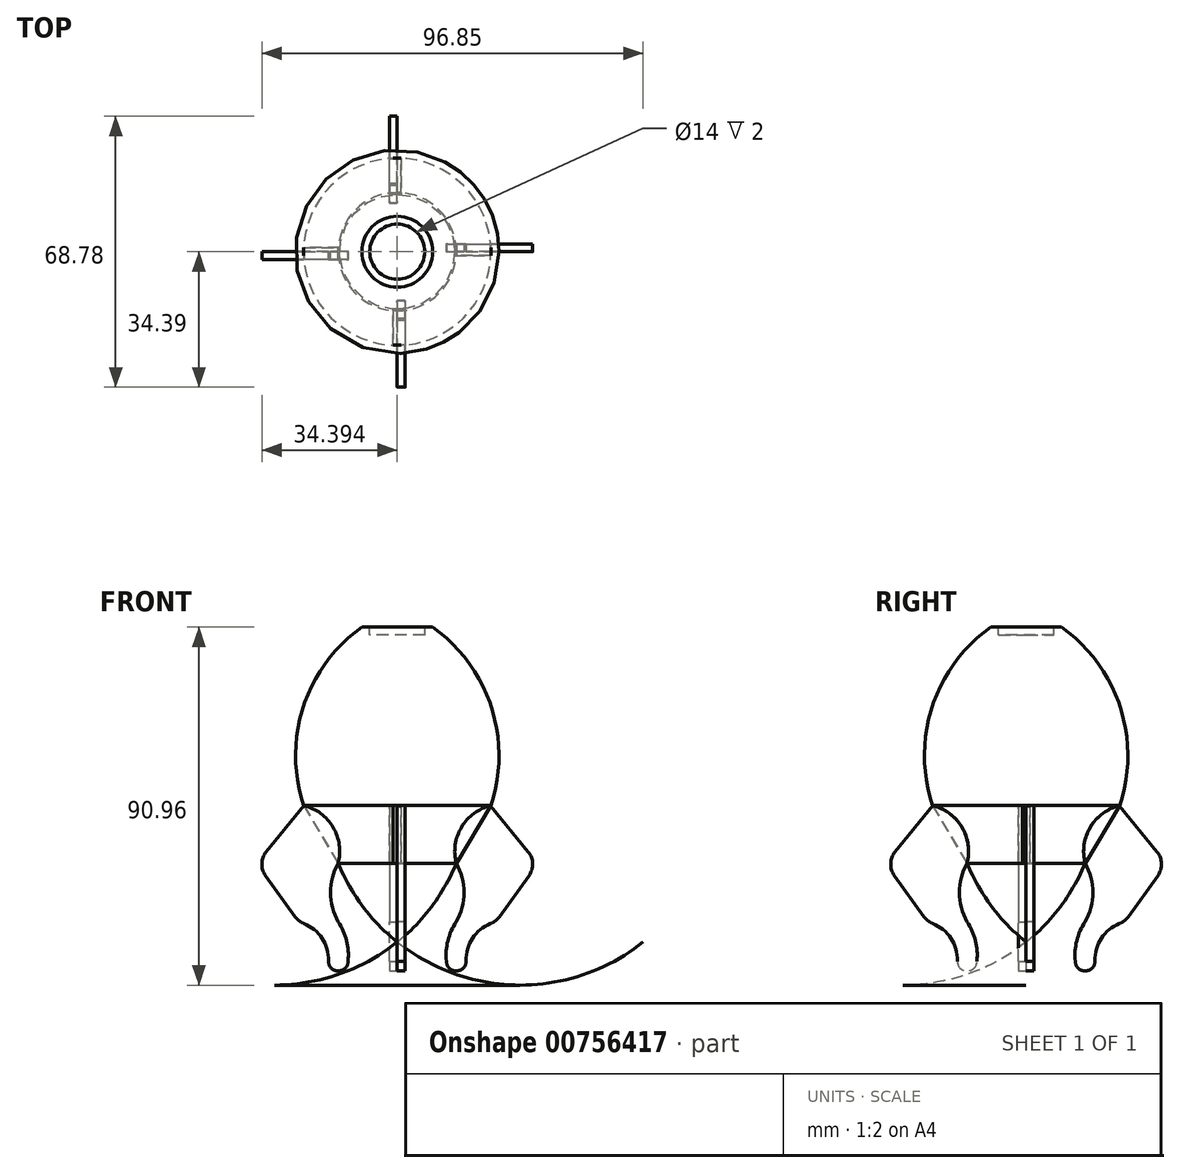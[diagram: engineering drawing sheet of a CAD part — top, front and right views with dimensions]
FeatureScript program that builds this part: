
annotation { "Feature Type Name" : "Feature", "Feature Type Description" : "" }
export const myFeature = defineFeature(function(context is Context, id is Id, definition is map)
    precondition{}
    {
        {
            var Q0;
            Q0=qCreatedBy(makeId("Front.planeOp"),FACE);
            var sketch = newSketch(context, id + "F0", { "sketchPlane" : qUnion([Q0])});
            skLineSegment(sketch, "E0", {"start": v(-18.64, 42.3) * mm, "end": v(-18.64, -37.7) * mm});
            skLineSegment(sketch, "E1", {"start": v(-18.64, 42.3) * mm, "end": v(-9.64, 42.3) * mm});
            skLineSegment(sketch, "E2", {"start": v(-18.64, -17.7) * mm, "end": v(-3.64, -17.7) * mm});
            skLineSegment(sketch, "E3", {"start": v(-18.64, -2.7) * mm, "end": v(5.24, -2.7) * mm});
            skArc(sketch, "E4", {"start": v(5.14, -3) * mm, "mid": v(5.24, 22.1) * mm, "end": v(-9.64, 42.3) * mm});
            skArc(sketch, "E5", {"start": v(-18.64, -37.7) * mm, "mid": v(-9.87, -28.65) * mm, "end": v(-3.64, -17.7) * mm});
            skArc(sketch, "E6", {"start": v(5.14, -3) * mm, "mid": v(-2.33, -8.51) * mm, "end": v(-3.64, -17.7) * mm});
            skLineSegment(sketch, "E7", {"start": v(-11.64, 42.3) * mm, "end": v(-11.64, 40.3) * mm});
            skLineSegment(sketch, "E8", {"start": v(-11.64, 40.3) * mm, "end": v(-18.64, 40.3) * mm});
            skSolve(sketch);
        }
        {
            var Q0;
            {var subQ2=sQuery(id+"F0.wireOp",EDGE,"E2");Q0=makeQuery(id+"F0.imprint","IMPRINT",FACE,{"disambiguationData":[TD([[makeQuery(id+"F0.imprint","IMPRINT",EDGE,{"derivedFrom":subQ2}),-1.0]])]});}
            var Q1;
            {var subQ3=sQuery(id+"F0.wireOp",EDGE,"E3");Q1=makeQuery(id+"F0.imprint","IMPRINT",FACE,{"disambiguationData":[TD([[makeQuery(id+"F0.imprint","IMPRINT",EDGE,{"derivedFrom":subQ3}),1.0]])]});}
            var Q2;
            {var subQ3=sQuery(id+"F0.wireOp",EDGE,"E2");Q2=makeQuery(id+"F0.imprint","IMPRINT",FACE,{"disambiguationData":[TD([[makeQuery(id+"F0.imprint","IMPRINT",EDGE,{"derivedFrom":subQ3}),1.0]])]});}
            var Q3;
            Q3=sQuery(id+"F0.wireOp",EDGE,"E0");
            revolve(context, id + "F1", {"surfaceOperationType" : NewSurfaceOperationType.NEW, "entities" : qUnion([Q0, Q1, Q2]), "axis" : qUnion([Q3]), "revolveType" : RevolveType.FULL});
        }
        {
            var Q0;
            Q0=qCreatedBy(makeId("Front.planeOp"),FACE);
            var sketch = newSketch(context, id + "F2", { "sketchPlane" : qUnion([Q0])});
            skLineSegment(sketch, "E9.0", {"start": v(-42.41, -3) * mm, "end": v(5.14, -3) * mm});
            skArc(sketch, "E10", {"start": v(-33.64, -17.7) * mm, "mid": v(-34.95, -8.51) * mm, "end": v(-42.41, -3) * mm});
            skLineSegment(sketch, "E11", {"start": v(-42.41, -3) * mm, "end": v(-33.64, -17.7) * mm});
            skSolve(sketch);
        }
        {
            var Q0;
            Q0 = qSketchRegion(id + "F2", true);
            extrude(context, id + "F3", {"entities" : qUnion([Q0]), "operationType" : NewBodyOperationType.ADD, "endBound" : BoundingType.SYMMETRIC, "depth" : 2 * mm, "offsetDistance" : 25 * mm});
        }
        {
            var Q0;
            Q0=qCreatedBy(makeId("Front.planeOp"),FACE);
            var sketch = newSketch(context, id + "F4", { "sketchPlane" : qUnion([Q0])});
            skLineSegment(sketch, "E12", {"start": v(-18.63, -37.56) * mm, "end": v(-18.63, -42.56) * mm});
            skLineSegment(sketch, "E13", {"start": v(-18.63, -42.56) * mm, "end": v(-33.63, -42.56) * mm});
            skLineSegment(sketch, "E14", {"start": v(-33.63, -42.56) * mm, "end": v(-33.63, -32.56) * mm});
            skLineSegment(sketch, "E15", {"start": v(-33.63, -32.56) * mm, "end": v(-43.63, -32.56) * mm});
            skArc(sketch, "E16", {"start": v(-36.13, -42.56) * mm, "mid": v(-33.63, -45.06) * mm, "end": v(-31.13, -42.56) * mm});
            skLineSegment(sketch, "E17", {"start": v(-33.63, -42.56) * mm, "end": v(-36.13, -42.56) * mm});
            skArc(sketch, "E18", {"start": v(-33.64, -17.7) * mm, "mid": v(-34.93, -8.54) * mm, "end": v(-42.34, -3.02) * mm});
            skLineSegment(sketch, "E19.0", {"start": v(-33.64, -17.7) * mm, "end": v(-3.64, -17.7) * mm});
            skArc(sketch, "E20", {"start": v(-33.64, -17.7) * mm, "mid": v(-35.6, -25.13) * mm, "end": v(-33.63, -32.56) * mm});
            skArc(sketch, "E21", {"start": v(-31.13, -42.56) * mm, "mid": v(-31.5, -37.34) * mm, "end": v(-33.63, -32.56) * mm});
            skArc(sketch, "E22", {"start": v(-36.13, -42.56) * mm, "mid": v(-37.75, -36.78) * mm, "end": v(-42.38, -32.97) * mm});
            skLineSegment(sketch, "E23", {"start": v(-42.34, -3.02) * mm, "end": v(-51.9, -14.78) * mm});
            skLineSegment(sketch, "E24", {"start": v(-52.08, -20.86) * mm, "end": v(-44.57, -31.26) * mm});
            skPoint(sketch, "E25.visualSharp", {"position": v(-54.33, -17.75) * mm});
            skArc(sketch, "E25.filletArc", {"start": v(-51.9, -14.78) * mm, "mid": v(-53.03, -17.8) * mm, "end": v(-52.08, -20.86) * mm});
            skPoint(sketch, "E26.visualSharp", {"position": v(-43.63, -32.56) * mm});
            skArc(sketch, "E26.filletArc", {"start": v(-44.57, -31.26) * mm, "mid": v(-43.6, -32.27) * mm, "end": v(-42.38, -32.97) * mm});
            skSolve(sketch);
        }
        {
            var Q0;
            {var subQ0=sQuery(id+"F4.wireOp",EDGE,"E14");Q0=makeQuery(id+"F4.imprint","IMPRINT",FACE,{"disambiguationData":[TD([[makeQuery(id+"F4.imprint","IMPRINT",EDGE,{"derivedFrom":subQ0}),-1.0]])]});}
            var Q1;
            {var subQ2=sQuery(id+"F4.wireOp",EDGE,"E16");Q1=makeQuery(id+"F4.imprint","IMPRINT",FACE,{"disambiguationData":[TD([[makeQuery(id+"F4.imprint","IMPRINT",EDGE,{"derivedFrom":subQ2}),1.0]])]});}
            var Q2;
            {var subQ2=sQuery(id+"F4.wireOp",EDGE,"E14");Q2=makeQuery(id+"F4.imprint","IMPRINT",FACE,{"disambiguationData":[TD([[makeQuery(id+"F4.imprint","IMPRINT",EDGE,{"derivedFrom":subQ2}),1.0]])]});}
            var Q3;
            Q3=makeQuery(id+"F4.imprint","IMPRINT",FACE,{"disambiguationData":[TD([[makeQuery(id+"F4.imprint","IMPRINT",EDGE,{"derivedFrom":sQuery(id+"F4.wireOp",EDGE,"E18")}),1.0]])]});
            extrude(context, id + "F5", {"entities" : qUnion([Q0, Q1, Q2, Q3]), "operationType" : NewBodyOperationType.ADD, "depth" : 2 * mm, "offsetDistance" : 25 * mm});
        }
        {
            var Q0;
            Q0=makeQuery(id+"F3.opExtrude","SWEPT_BODY",BODY,{"disambiguationData":[OSD([sQuery(id+"F2.wireOp",EDGE,"E10"),sQuery(id+"F2.wireOp",EDGE,"E11")])]});
            var Q1;
            Q1=makeQuery(id+"F1.opRevolve","SWEPT_FACE",FACE,{"disambiguationData":[OSD([sQuery(id+"F0.wireOp",EDGE,"E5")])]});
            circularPattern(context, id + "F6", {"entities" : qUnion([Q0]), "axis" : qUnion([Q1]), "angle" : 360 * degree, "instanceCount" : 4, "equalSpace" : true});
        }
    });
